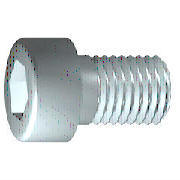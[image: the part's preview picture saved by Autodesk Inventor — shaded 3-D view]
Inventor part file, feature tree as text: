
AUTODESK INVENTOR PART (.ipt)
format: ipt  version: 2024.2 (Build 282272000, 272)  size: 198,656 bytes
history: native  units: mm (DEFAULTED — no unit token found)
features: extrude x1, plane x1, fillet x1
ambient origin geometry x7: Origin, YZ Plane, XY Plane, X Axis, Y Axis, Z Axis, Center Point
bodies: Solid1 (feature_tree), Body (feature_tree)
feature tree (3):
  extrude  "Slot"  Depth=5.0mm
  plane  "Work Plane1"
  fillet  "Fillet2"  Radius=0.24548mm
